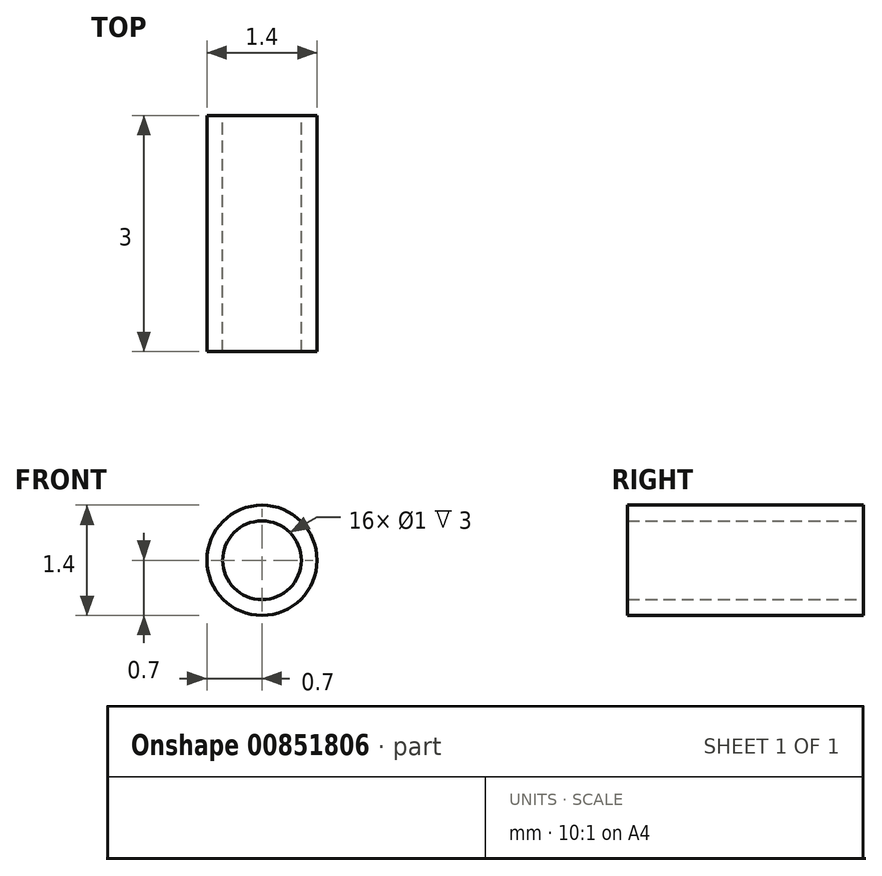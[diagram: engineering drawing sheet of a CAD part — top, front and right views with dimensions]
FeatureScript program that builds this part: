
annotation { "Feature Type Name" : "Feature", "Feature Type Description" : "" }
export const myFeature = defineFeature(function(context is Context, id is Id, definition is map)
    precondition{}
    {
        {
            var Q0;
            Q0=qCreatedBy(makeId("Front.planeOp"),FACE);
            var sketch = newSketch(context, id + "F0", { "sketchPlane" : qUnion([Q0])});
            skCircle(sketch, "E0", {"center": v(0, 0) * mm, "radius": 0.7 * mm});
            skCircle(sketch, "E1", {"center": v(0, 0) * mm, "radius": 0.5 * mm});
            skSolve(sketch);
        }
        {
            var Q0;
            Q0 = qSketchRegion(id + "F0", true);
            extrude(context, id + "F1", {"entities" : qUnion([Q0]), "endBound" : BoundingType.SYMMETRIC, "depth" : 3 * mm, "offsetDistance" : 25.4 * mm});
        }
    });
